# Revit family: Tablex LED
name_source: partatom
category: Осветительные приборы
revit_build: Autodesk Revit 2018 (Build: 20180423_1000(x64)
units: mm (PartAtom-declared; Revit-internal decimal feet)

## family parameters
Источник света = Нет
Общий = Нет
Основа = Грань
При загрузке вырезать с полостями = Нет
Размер круглого соединителя = Использовать диаметр
Тип детали = Нормальный
Точка расчета площади = Нет

## types (2) — shared parameters
ADSK_Версия Revit = 2018
ADSK_Версия семейства = 1.01
ADSK_Единица измерения = шт.
ADSK_Классификация нагрузок = Освещение
ADSK_Количество = 1
ADSK_Количество фаз = 1
ADSK_Коэффициент мощности = 0.95
ADSK_Масса = 5.8
ADSK_Материал = Литой алюминий
ADSK_Номинальная мощность = 10 Вт
ADSK_Полная мощность = 11 В·А
ADSK_Размер_Высота = 110 мм
ADSK_Размер_Длина = 394 мм
ADSK_Размер_Ширина = 228 мм
ADSK_Ток = 0 А
IP = 67
URL = https://galad.ru
Блок аварийного питания = Нет
Группа модели = Светильники
Класс защиты от поражения электрическим током = 1
Климатическое исполнение = -60…55 °С
Маркировка по газу = 1Ex db mb IIC T6 Gb X
Маркировка по пыли = Ex td IIIC T65°C Db X
Область использования = Взрывозащита
Описание = Серия включает в себя световые табло как с простой, так и с комплексной надписью на одном рассеивателе. Табло TablEx имеет комбинированный вид взрывозащиты db взрывонепроницаемая оболочка для коммутационного отсека источника питания и mb – заливка компаундом для светооптического отсека, маркировку взрывозащиты 1Ex db mb IIC и предназначен для работы во взрывоопасных зон классов 1 и 2 в помещениях и на открытых площадках.
Полная установленная мощность = 11 В·А
Срок службы = 10 лет
Тип ПРА = ЭПРА
Тип источника света = LED
Тип крепления = Скоба
Тип монтажной поверхности = Пристраиваемый
Тип продукции = Взрывозащищенный светильник
Тип устройства управления светодиодами = без управления
Частота = 50
zero-valued in all types: Отметка по умолчанию

## per-type parameters (varying)
| type | ADSK_Код изделия | ADSK_Напряжение | ADSK_Обозначение | Климатическая зона |
| TABLEX-10-024-З-Б-20-О-ВЫХОД | 21094 | 24 В | ГОСТ IEC 60598-1, ГОСТ 17516.1, ГОСТ 15150, ГОСТ IEC 60598-2-5, ГОСТ IEC 60079-10-1-20012 | ОМ1
УХЛ2 |
| TABLEX-10-230-З-Б-20-О-ВЫХОД | 21093 | 230 В | ГОСТ IEC 60598-1, ГОСТ 17516.1, ГОСТ 15150, ГОСТ IEC 60598-2-5, ГОСТ IEC 60079-10-1-20011 | ОМ1
УХЛ1 |

note: column(s) folded — value = type name in every type: ADSK_Марка, ADSK_Наименование, ADSK_Наименование краткое
